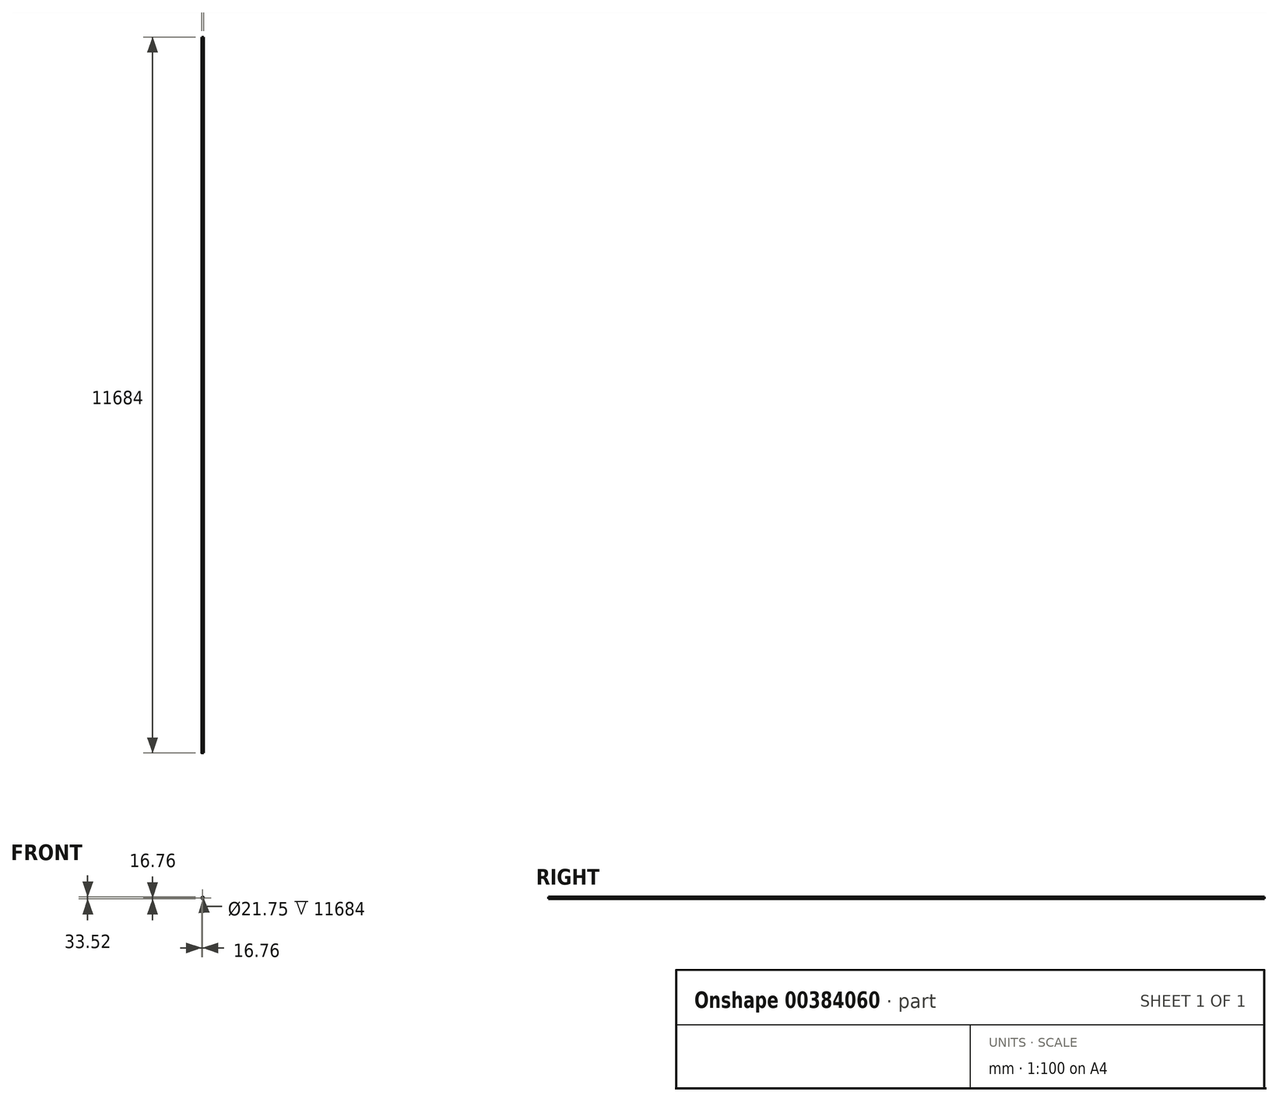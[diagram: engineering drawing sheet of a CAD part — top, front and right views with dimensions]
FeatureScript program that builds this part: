
annotation { "Feature Type Name" : "Feature", "Feature Type Description" : "" }
export const myFeature = defineFeature(function(context is Context, id is Id, definition is map)
    precondition{}
    {
        {
            var Q0;
            Q0=qCreatedBy(makeId("Front.planeOp"),FACE);
            var sketch = newSketch(context, id + "F0", { "sketchPlane" : qUnion([Q0])});
            skCircle(sketch, "E0", {"center": v(0, 0) * mm, "radius": 16.76 * mm});
            skCircle(sketch, "E1", {"center": v(0, 0) * mm, "radius": 10.87 * mm});
            skSolve(sketch);
        }
        {
            var Q0;
            Q0=makeQuery(id+"F0.imprint","IMPRINT",FACE,{"disambiguationData":[TD([[makeQuery(id+"F0.imprint","IMPRINT",EDGE,{"derivedFrom":sQuery(id+"F0.wireOp",EDGE,"E0")}),1.0]])]});
            extrude(context, id + "F1", {"entities" : qUnion([Q0]), "depth" : 11684 * mm});
        }
    });
